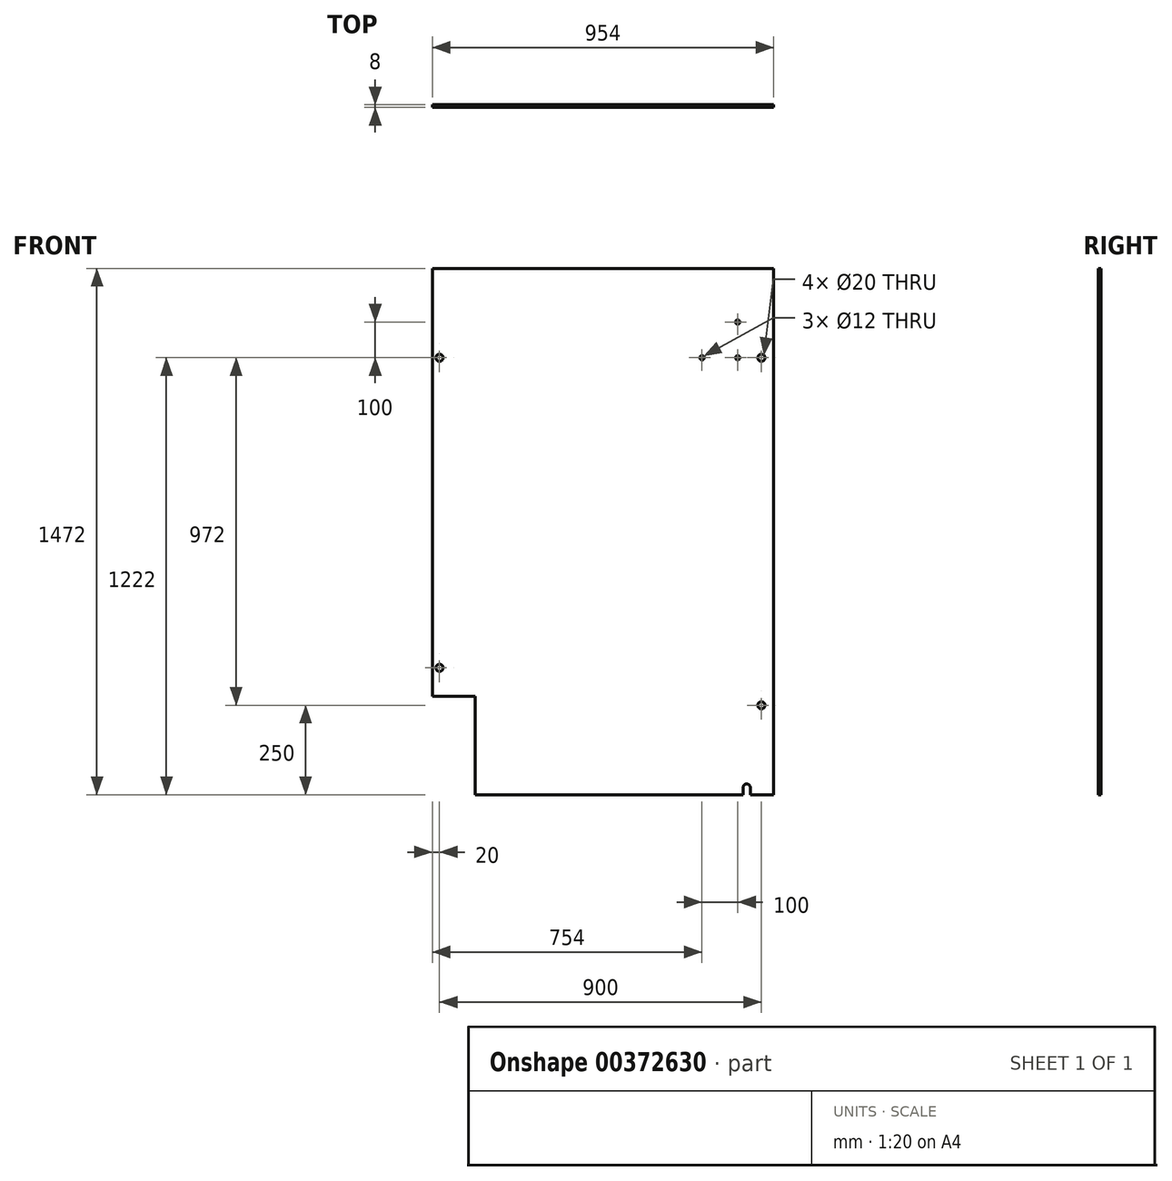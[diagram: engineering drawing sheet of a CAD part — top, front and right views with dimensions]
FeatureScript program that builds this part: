
annotation { "Feature Type Name" : "Feature", "Feature Type Description" : "" }
export const myFeature = defineFeature(function(context is Context, id is Id, definition is map)
    precondition{}
    {
        {
            var Q0;
            Q0=qCreatedBy(makeId("Front.planeOp"),FACE);
            var sketch = newSketch(context, id + "F0", { "sketchPlane" : qUnion([Q0])});
            skLineSegment(sketch, "E0.bottom", {"start": v(-477, 736) * mm, "end": v(477, 736) * mm});
            skLineSegment(sketch, "E0.top", {"start": v(-477, -736) * mm, "end": v(392, -736) * mm, "construction": true});
            skLineSegment(sketch, "E0.left", {"start": v(-477, 736) * mm, "end": v(-477, -736) * mm, "construction": true});
            skLineSegment(sketch, "E0.right", {"start": v(477, 736) * mm, "end": v(477, -736) * mm});
            skPoint(sketch, "E0.middle", {"position": v(0, 0) * mm});
            skCircle(sketch, "E1", {"center": v(-457, 486) * mm, "radius": 10 * mm});
            skCircle(sketch, "E2", {"center": v(-457, -381) * mm, "radius": 10 * mm});
            skCircle(sketch, "E3", {"center": v(443, -486) * mm, "radius": 10 * mm});
            skCircle(sketch, "E4", {"center": v(443, 486) * mm, "radius": 10 * mm});
            skCircle(sketch, "E5", {"center": v(377, 486) * mm, "radius": 6 * mm});
            skCircle(sketch, "E6", {"center": v(277, 486) * mm, "radius": 6 * mm});
            skCircle(sketch, "E7", {"center": v(377, 586) * mm, "radius": 6 * mm});
            skArc(sketch, "E8", {"start": v(412, -716) * mm, "mid": v(402, -706) * mm, "end": v(392, -716) * mm});
            skLineSegment(sketch, "E9", {"start": v(-457, 486) * mm, "end": v(-457, -381) * mm, "construction": true});
            skLineSegment(sketch, "E10", {"start": v(-457, 486) * mm, "end": v(0, 486) * mm, "construction": true});
            skLineSegment(sketch, "E11", {"start": v(0, 486) * mm, "end": v(277, 486) * mm, "construction": true});
            skLineSegment(sketch, "E12", {"start": v(277, 486) * mm, "end": v(377, 486) * mm, "construction": true});
            skLineSegment(sketch, "E13", {"start": v(377, 486) * mm, "end": v(443, 486) * mm, "construction": true});
            skLineSegment(sketch, "E14", {"start": v(443, 486) * mm, "end": v(443, -486) * mm, "construction": true});
            skLineSegment(sketch, "E15", {"start": v(-477, 736) * mm, "end": v(-477, -461) * mm});
            skLineSegment(sketch, "E16", {"start": v(-477, -461) * mm, "end": v(-357, -461) * mm});
            skLineSegment(sketch, "E17", {"start": v(-357, -461) * mm, "end": v(-357, -736) * mm});
            skLineSegment(sketch, "E18", {"start": v(-357, -736) * mm, "end": v(392, -736) * mm});
            skLineSegment(sketch, "E19", {"start": v(412, -716) * mm, "end": v(412, -736) * mm});
            skLineSegment(sketch, "E20", {"start": v(392, -716) * mm, "end": v(392, -736) * mm});
            skLineSegment(sketch, "E21.trimOffspring", {"start": v(412, -736) * mm, "end": v(477, -736) * mm, "construction": true});
            skLineSegment(sketch, "E22.trimOffspring", {"start": v(412, -736) * mm, "end": v(477, -736) * mm});
            skSolve(sketch);
        }
        {
            var Q0;
            Q0 = qSketchRegion(id + "F0", true);
            extrude(context, id + "F1", {"entities" : qUnion([Q0]), "depth" : 8 * mm});
        }
    });
